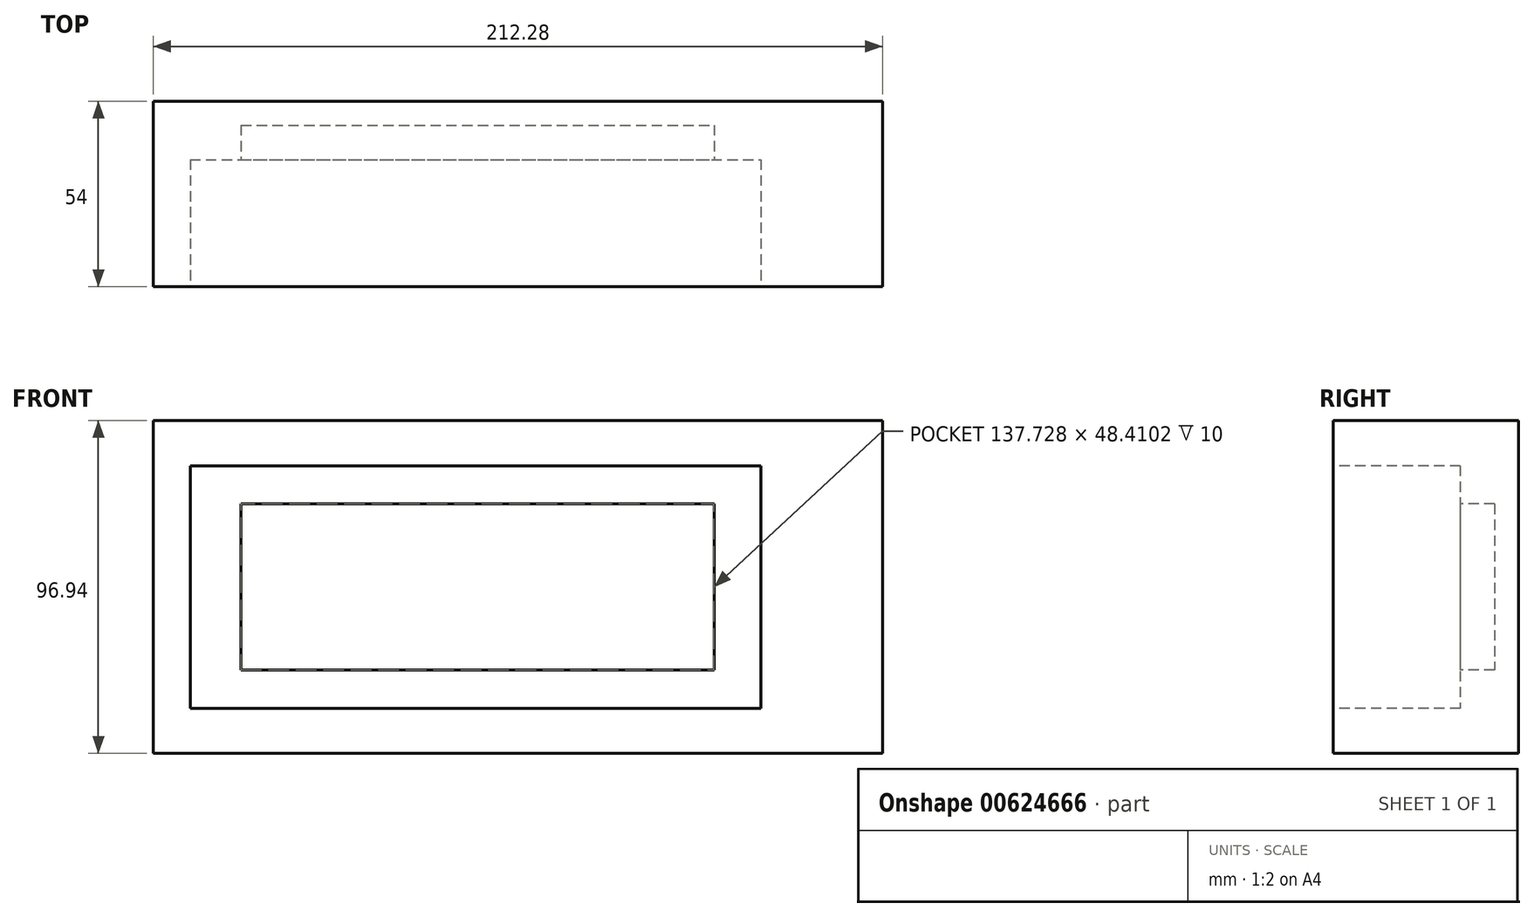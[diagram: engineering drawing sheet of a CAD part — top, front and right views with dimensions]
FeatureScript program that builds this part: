
annotation { "Feature Type Name" : "Feature", "Feature Type Description" : "" }
export const myFeature = defineFeature(function(context is Context, id is Id, definition is map)
    precondition{}
    {
        {
            var Q0;
            Q0=qCreatedBy(makeId("Front.planeOp"),FACE);
            var sketch = newSketch(context, id + "F0", { "sketchPlane" : qUnion([Q0])});
            skLineSegment(sketch, "E0.bottom", {"start": v(-106.14, 48.47) * mm, "end": v(106.14, 48.47) * mm});
            skLineSegment(sketch, "E0.top", {"start": v(-106.14, -48.47) * mm, "end": v(106.14, -48.47) * mm});
            skLineSegment(sketch, "E0.left", {"start": v(-106.14, 48.47) * mm, "end": v(-106.14, -48.47) * mm});
            skLineSegment(sketch, "E0.right", {"start": v(106.14, 48.47) * mm, "end": v(106.14, -48.47) * mm});
            skPoint(sketch, "E0.middle", {"position": v(0, 0) * mm});
            skSolve(sketch);
        }
        {
            var Q0;
            Q0=makeQuery(id+"F0.imprint","IMPRINT",FACE,{"disambiguationData":[TD([[makeQuery(id+"F0.imprint","IMPRINT",EDGE,{"derivedFrom":sQuery(id+"F0.wireOp",EDGE,"E0.bottom")}),-1.0]])]});
            extrude(context, id + "F1", {"entities" : qUnion([Q0]), "depth" : 54 * mm, "offsetDistance" : 25 * mm});
        }
        {
            var Q0;
            Q0=makeQuery(id+"F1.opExtrude","CAP_FACE",FACE,{"disambiguationData":[OSD([sQuery(id+"F0.wireOp",EDGE,"E0.bottom"),sQuery(id+"F0.wireOp",EDGE,"E0.top"),sQuery(id+"F0.wireOp",EDGE,"E0.left"),sQuery(id+"F0.wireOp",EDGE,"E0.right")])],"isStart":false});
            var sketch = newSketch(context, id + "F2", { "sketchPlane" : qUnion([Q0])});
            skLineSegment(sketch, "E1.bottom", {"start": v(-95.45, 35.3) * mm, "end": v(70.73, 35.3) * mm});
            skLineSegment(sketch, "E1.top", {"start": v(-95.45, -35.3) * mm, "end": v(70.73, -35.3) * mm});
            skLineSegment(sketch, "E1.left", {"start": v(-95.45, 35.3) * mm, "end": v(-95.45, -35.3) * mm});
            skLineSegment(sketch, "E1.right", {"start": v(70.73, 35.3) * mm, "end": v(70.73, -35.3) * mm});
            skPoint(sketch, "E1.middle", {"position": v(-12.36, 0) * mm});
            skSolve(sketch);
        }
        {
            var Q0;
            Q0=makeQuery(id+"F2.imprint","IMPRINT",FACE,{"disambiguationData":[TD([[makeQuery(id+"F2.imprint","IMPRINT",EDGE,{"derivedFrom":sQuery(id+"F2.wireOp",EDGE,"E1.bottom")}),-1.0]])]});
            var sketch = newSketch(context, id + "F3", { "sketchPlane" : qUnion([Q0])});
            skLineSegment(sketch, "E2.bottom", {"start": v(61.06, -26.52) * mm, "end": v(-89.2, -26.52) * mm});
            skLineSegment(sketch, "E2.top", {"start": v(61.06, 26.52) * mm, "end": v(-89.2, 26.52) * mm});
            skLineSegment(sketch, "E2.left", {"start": v(61.06, -26.52) * mm, "end": v(61.06, 26.52) * mm});
            skLineSegment(sketch, "E2.right", {"start": v(-89.2, -26.52) * mm, "end": v(-89.2, 26.52) * mm});
            skPoint(sketch, "E2.middle", {"position": v(-14.07, 0) * mm});
            skSolve(sketch);
        }
        {
            var Q0;
            Q0=makeQuery(id+"F2.imprint","IMPRINT",FACE,{"disambiguationData":[TD([[makeQuery(id+"F2.imprint","IMPRINT",EDGE,{"derivedFrom":sQuery(id+"F2.wireOp",EDGE,"E1.bottom")}),-1.0]])]});
            extrude(context, id + "F4", {"entities" : qUnion([Q0]), "operationType" : NewBodyOperationType.REMOVE, "oppositeDirection" : true, "depth" : 37 * mm, "offsetDistance" : 25 * mm});
        }
        {
            var Q0;
            Q0=makeQuery(id+"F3.imprint","IMPRINT",FACE,{"disambiguationData":[TD([[makeQuery(id+"F3.imprint","IMPRINT",EDGE,{"derivedFrom":sQuery(id+"F3.wireOp",EDGE,"E2.bottom")}),-1.0]])]});
            var sketch = newSketch(context, id + "F5", { "sketchPlane" : qUnion([Q0])});
            skLineSegment(sketch, "E3.bottom", {"start": v(-80.66, 24.2) * mm, "end": v(57.07, 24.2) * mm});
            skLineSegment(sketch, "E3.top", {"start": v(-80.66, -24.2) * mm, "end": v(57.07, -24.2) * mm});
            skLineSegment(sketch, "E3.left", {"start": v(-80.66, 24.2) * mm, "end": v(-80.66, -24.2) * mm});
            skLineSegment(sketch, "E3.right", {"start": v(57.07, 24.2) * mm, "end": v(57.07, -24.2) * mm});
            skPoint(sketch, "E3.middle", {"position": v(-11.8, 0) * mm});
            skSolve(sketch);
        }
        {
            var Q0;
            Q0=makeQuery(id+"F5.imprint","IMPRINT",FACE,{"disambiguationData":[TD([[makeQuery(id+"F5.imprint","IMPRINT",EDGE,{"derivedFrom":sQuery(id+"F5.wireOp",EDGE,"E3.bottom")}),-1.0]])]});
            extrude(context, id + "F6", {"entities" : qUnion([Q0]), "operationType" : NewBodyOperationType.REMOVE, "oppositeDirection" : true, "depth" : 47 * mm, "offsetDistance" : 25 * mm});
        }
    });
